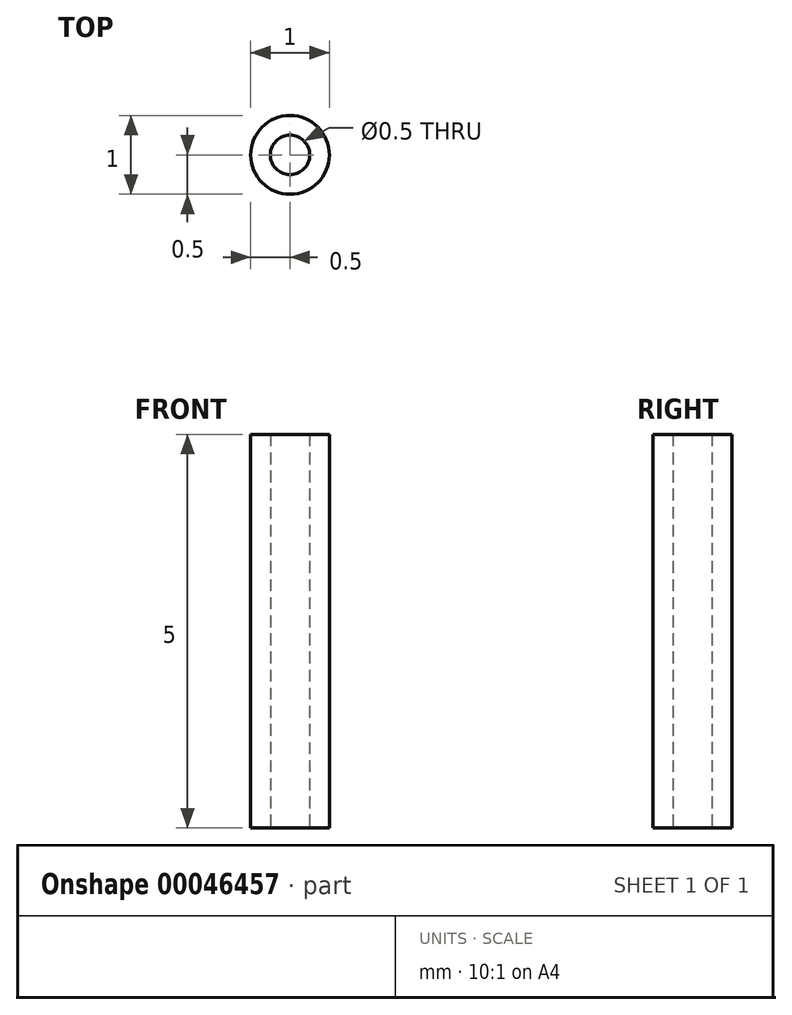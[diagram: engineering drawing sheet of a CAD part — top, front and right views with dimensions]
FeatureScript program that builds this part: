
annotation { "Feature Type Name" : "Feature", "Feature Type Description" : "" }
export const myFeature = defineFeature(function(context is Context, id is Id, definition is map)
    precondition{}
    {
        {
            var Q0;
            Q0=qCreatedBy(makeId("Top.planeOp"),FACE);
            var sketch = newSketch(context, id + "F0", { "sketchPlane" : qUnion([Q0])});
            skCircle(sketch, "E0", {"center": v(0, 0) * mm, "radius": 0.25 * mm});
            skCircle(sketch, "E1", {"center": v(0, 0) * mm, "radius": 0.5 * mm});
            skSolve(sketch);
        }
        {
            var Q0;
            Q0=makeQuery(id+"F0.imprint","IMPRINT",FACE,{"disambiguationData":[TD([[makeQuery(id+"F0.imprint","IMPRINT",EDGE,{"derivedFrom":sQuery(id+"F0.wireOp",EDGE,"E0")}),-1.0]])]});
            extrude(context, id + "F1", {"entities" : qUnion([Q0]), "depth" : 5 * mm});
        }
    });
